# Revit family: P190780JX-084c_JGRP636HL_StainlessSteel_JA_Cooking_Rangetop
name_source: partatom
category: Specialty Equipment
units: mm (PartAtom-declared; Revit-internal decimal feet)

## family parameters
Always vertical = Yes
Cut with Voids When Loaded = No
Enable Cutting in Views = No
Maintain Annotation Orientation = No
Part Type = Normal
Room Calculation Point = No
Round Connector Dimension = Use Diameter
Shared = No
Work Plane-Based = No

## types (1)
- JGRP636HL
    Amps = 0 A
    Body Material = ARCAT - Metal - Steel - Stainless
    Clearance Material = ARCAT - Clearance
    Connector Material = ARCAT - Metal - Cast Iron
    Cooking Grate Material = ARCAT - Metal - Cast Iron 1/4" Plate
    Default Elevation = 0"
    Depth = 29 13/16"
    Description = RISE™ 36" Gas Professional-Style Range with Grill
Cuisinière au gaz de style professionnel RISE™, 36 po
    Dimension Guide = https://www.whirlpool.com
https://www.whirlpool.com
    Door Material = ARCAT - Metal - Steel - Stainless
    Family Name = 36” GAS COMMERCIAL RANGES
    Feature 1 = 34 Range Configurations
34 configurations de cuisinière
    Feature 2 = Flat Tine Racks
Tiges de grille plates
    Feature 3 = Remote Access
Accès à distance
    Glass Material = ARCAT - Glass - Tempered - Black
    Handle Material = ARCAT - Metal - Steel - Gray
    Height = 38 3/4"
    Installation-Fabrication = http://access.whirlpool.com Instruction&sku=JGRP636HL&language=EN
http://access.whirlpool.com Instruction&sku=JGRP636HL&language=FR
    Knob Material = ARCAT - Metal - Steel - Stainless
    Leg Material = ARCAT - Plastic - Black
    Manufacturer = Jenn Air
    Model = JGRP636HL
    Voltage = 0 V
    Width = 35 7/8"

## geometry (parser evidence)
native form markers: Sweep x4
no freeform markers — native parametric forms only
